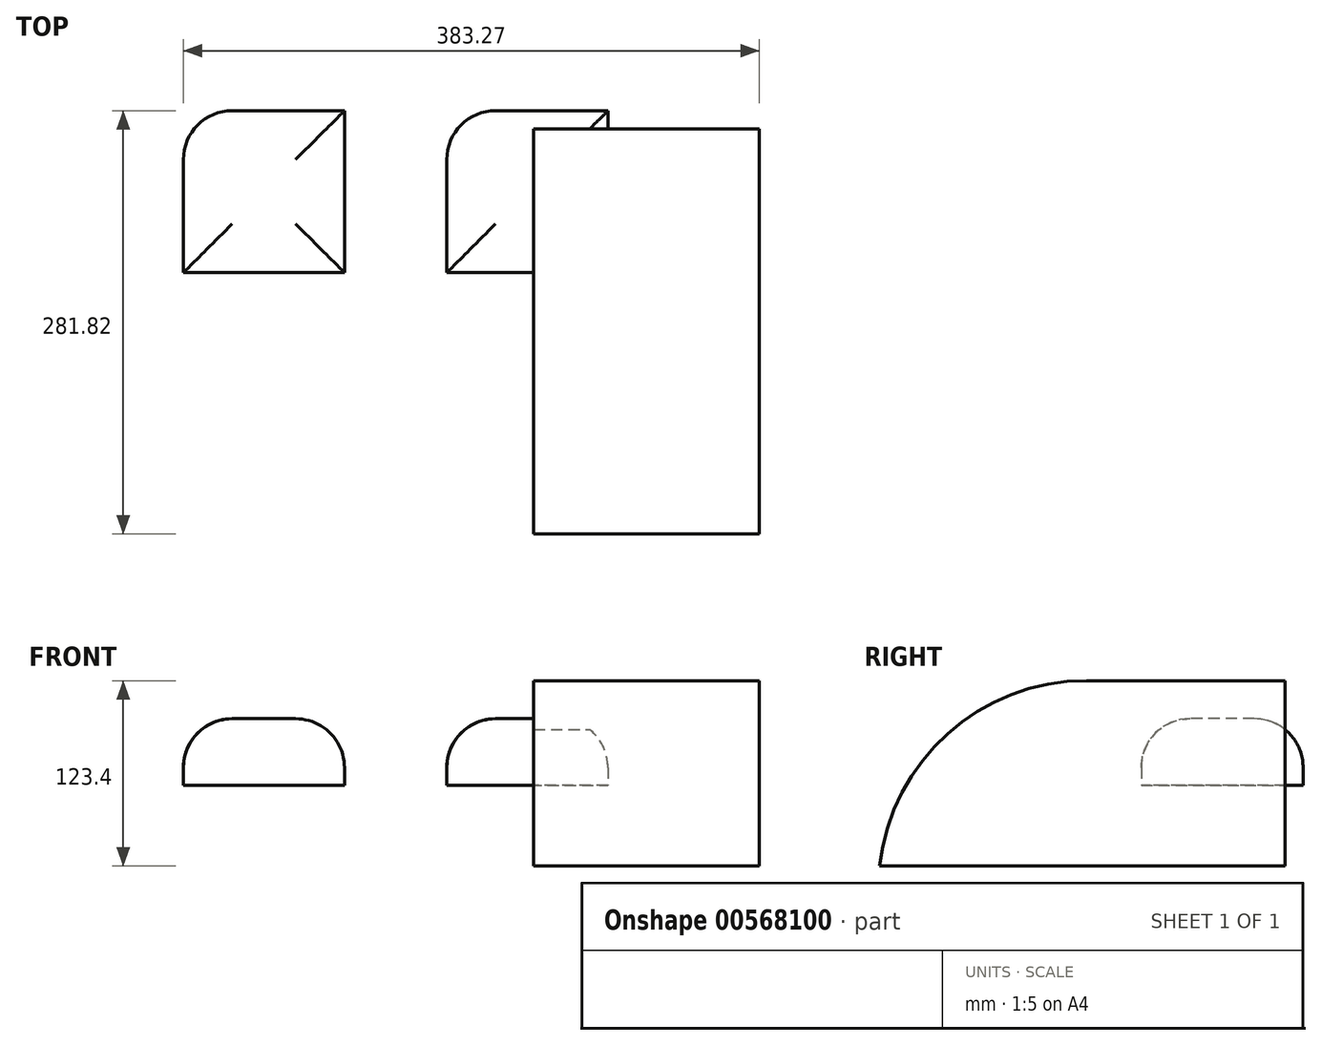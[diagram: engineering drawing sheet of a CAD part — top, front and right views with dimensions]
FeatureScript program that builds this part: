
annotation { "Feature Type Name" : "Feature", "Feature Type Description" : "" }
export const myFeature = defineFeature(function(context is Context, id is Id, definition is map)
    precondition{}
    {
        {
            var Q0;
            Q0=qCreatedBy(makeId("Top.planeOp"),FACE);
            var sketch = newSketch(context, id + "F0", { "sketchPlane" : qUnion([Q0])});
            skLineSegment(sketch, "E0.bottom", {"start": v(-57.9, 67.47) * mm, "end": v(49.3, 67.47) * mm});
            skLineSegment(sketch, "E0.top", {"start": v(-57.9, -40.27) * mm, "end": v(49.3, -40.27) * mm});
            skLineSegment(sketch, "E0.left", {"start": v(-57.9, 67.47) * mm, "end": v(-57.9, -40.27) * mm});
            skLineSegment(sketch, "E0.right", {"start": v(49.3, 67.47) * mm, "end": v(49.3, -40.27) * mm});
            skSolve(sketch);
        }
        {
            var Q0;
            Q0=makeQuery(id+"F0.imprint","IMPRINT",FACE,{"disambiguationData":[TD([[makeQuery(id+"F0.imprint","IMPRINT",EDGE,{"derivedFrom":sQuery(id+"F0.wireOp",EDGE,"E0.bottom")}),-1.0]])]});
            extrude(context, id + "F1", {"entities" : qUnion([Q0]), "depth" : 44.45 * mm, "offsetDistance" : 25.4 * mm});
        }
        {
            var Q0;
            Q0=makeQuery(id+"F1.opExtrude","SWEPT_EDGE",EDGE,{"disambiguationData":[OSD([sQuery(id+"F0.wireOp",EDGE,"E0.bottom"),sQuery(id+"F0.wireOp",EDGE,"E0.left")])]});
            var Q1;
            Q1=makeQuery(id+"F1.opExtrude","CAP_FACE",FACE,{"disambiguationData":[OSD([sQuery(id+"F0.wireOp",EDGE,"E0.bottom"),sQuery(id+"F0.wireOp",EDGE,"E0.top"),sQuery(id+"F0.wireOp",EDGE,"E0.left"),sQuery(id+"F0.wireOp",EDGE,"E0.right")])],"isStart":false});
            fillet(context, id + "F2", {"entities" : qUnion([Q0, Q1]), "radius" : 32.5 * mm, "tangentPropagation" : true, "allowEdgeOverflow" : false});
        }
        {
            var Q0;
            Q0=makeQuery(id+"F1.opExtrude","SWEPT_BODY",BODY,{"disambiguationData":[OSD([sQuery(id+"F0.wireOp",EDGE,"E0.bottom"),sQuery(id+"F0.wireOp",EDGE,"E0.top"),sQuery(id+"F0.wireOp",EDGE,"E0.left"),sQuery(id+"F0.wireOp",EDGE,"E0.right")])]});
            transform(context, id + "F3", {"entities" : qUnion([Q0]), "transformType" : TransformType.TRANSLATION_3D, "dx" : -175.26 * mm, "dy" : 0 * mm, "dz" : 0 * mm, "makeCopy" : true});
        }
        {
            var Q0;
            Q0=qCreatedBy(makeId("Right.planeOp"),FACE);
            var sketch = newSketch(context, id + "F4", { "sketchPlane" : qUnion([Q0])});
            skLineSegment(sketch, "E1.bottom", {"start": v(-214.35, 69.77) * mm, "end": v(55.4, 69.77) * mm});
            skLineSegment(sketch, "E1.top", {"start": v(-214.35, -53.63) * mm, "end": v(55.4, -53.63) * mm});
            skLineSegment(sketch, "E1.left", {"start": v(-214.35, 69.77) * mm, "end": v(-214.35, -53.63) * mm});
            skLineSegment(sketch, "E1.right", {"start": v(55.4, 69.77) * mm, "end": v(55.4, -53.63) * mm});
            skSolve(sketch);
        }
        {
            var Q0;
            Q0=makeQuery(id+"F4.imprint","IMPRINT",FACE,{"disambiguationData":[TD([[makeQuery(id+"F4.imprint","IMPRINT",EDGE,{"derivedFrom":sQuery(id+"F4.wireOp",EDGE,"E1.bottom")}),-1.0]])]});
            extrude(context, id + "F5", {"entities" : qUnion([Q0]), "operationType" : NewBodyOperationType.ADD, "depth" : 150.11 * mm, "offsetDistance" : 25.4 * mm});
        }
        {
            var Q0;
            Q0=makeQuery(id+"F5.opExtrude","SWEPT_EDGE",EDGE,{"disambiguationData":[OSD([sQuery(id+"F4.wireOp",EDGE,"E1.bottom"),sQuery(id+"F4.wireOp",EDGE,"E1.left")])]});
            fillet(context, id + "F6", {"entities" : qUnion([Q0]), "radius" : 138.6 * mm, "tangentPropagation" : true, "allowEdgeOverflow" : false});
        }
    });
